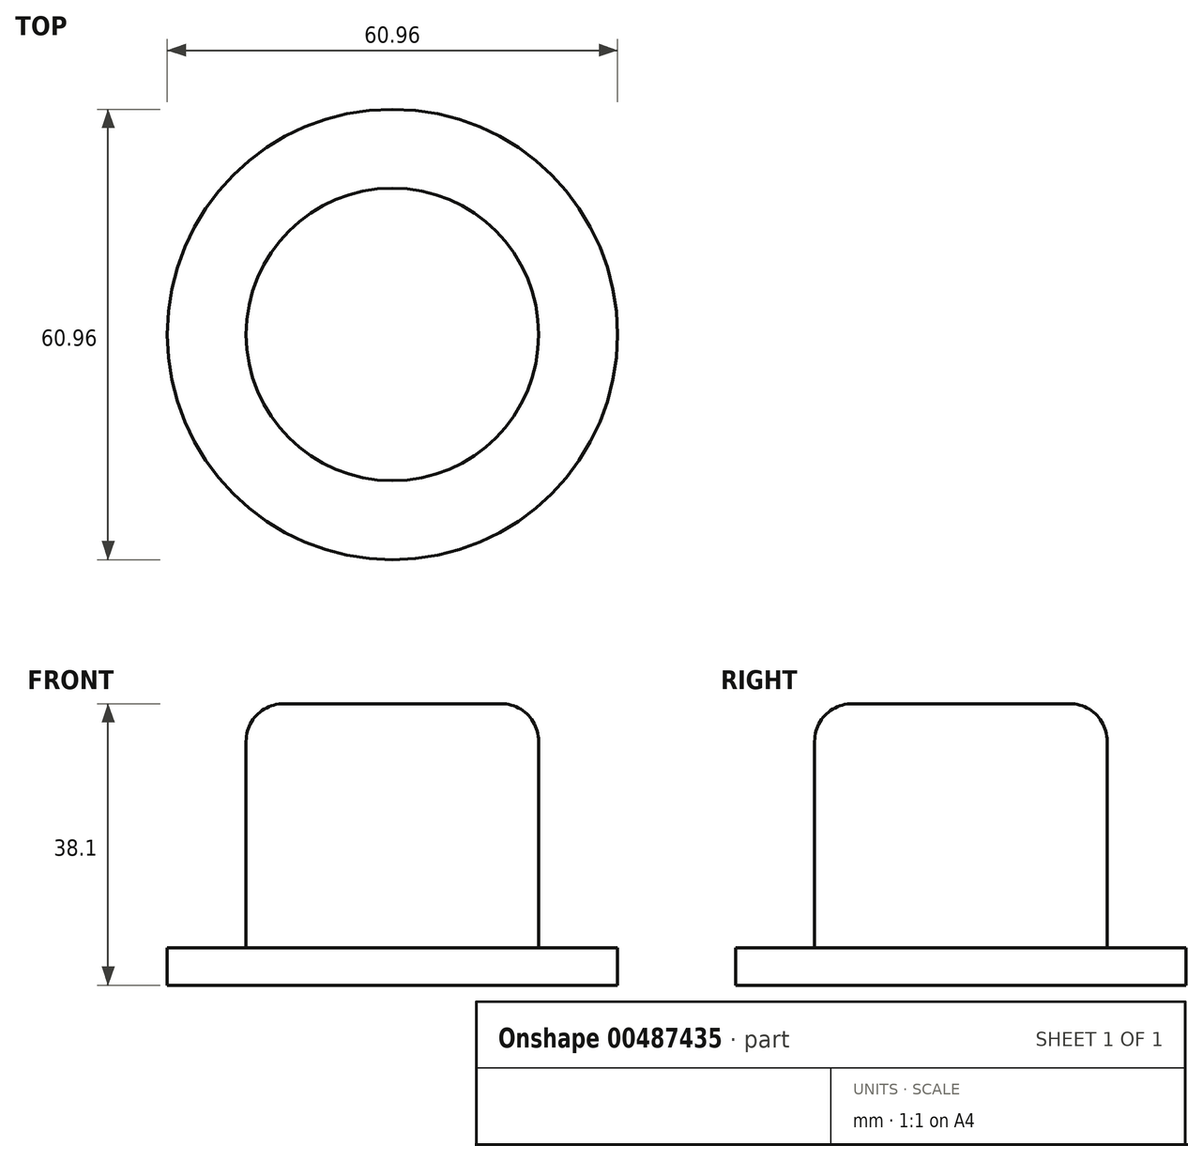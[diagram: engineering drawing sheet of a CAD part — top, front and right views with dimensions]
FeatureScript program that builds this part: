
annotation { "Feature Type Name" : "Feature", "Feature Type Description" : "" }
export const myFeature = defineFeature(function(context is Context, id is Id, definition is map)
    precondition{}
    {
        {
            var Q0;
            Q0=qCreatedBy(makeId("Front.planeOp"),FACE);
            var sketch = newSketch(context, id + "F0", { "sketchPlane" : qUnion([Q0])});
            skLineSegment(sketch, "E0", {"start": v(-30.48, 0) * mm, "end": v(-30.48, 5.08) * mm});
            skLineSegment(sketch, "E1", {"start": v(-19.8, 5.08) * mm, "end": v(-19.8, 38.1) * mm});
            skLineSegment(sketch, "E2", {"start": v(-19.8, 38.1) * mm, "end": v(0, 38.1) * mm});
            skLineSegment(sketch, "E3", {"start": v(-30.48, 5.08) * mm, "end": v(-19.8, 5.08) * mm});
            skLineSegment(sketch, "E4", {"start": v(-30.48, 0) * mm, "end": v(0, 0) * mm});
            skLineSegment(sketch, "E5", {"start": v(0, 0) * mm, "end": v(0, 38.1) * mm});
            skSolve(sketch);
        }
        {
            var Q0;
            Q0 = qSketchRegion(id + "F0", true);
            var Q1;
            Q1=sQuery(id+"F0.wireOp",EDGE,"E5");
            revolve(context, id + "F1", {"entities" : qUnion([Q0]), "axis" : qUnion([Q1]), "revolveType" : RevolveType.FULL});
        }
        {
            var Q0;
            Q0=makeQuery(id+"F1.opRevolve","SWEPT_FACE",FACE,{"disambiguationData":[OSD([sQuery(id+"F0.wireOp",EDGE,"E2")])]});
            fillet(context, id + "F2", {"entities" : qUnion([Q0]), "radius" : 5.08 * mm, "tangentPropagation" : true, "allowEdgeOverflow" : false});
        }
    });
